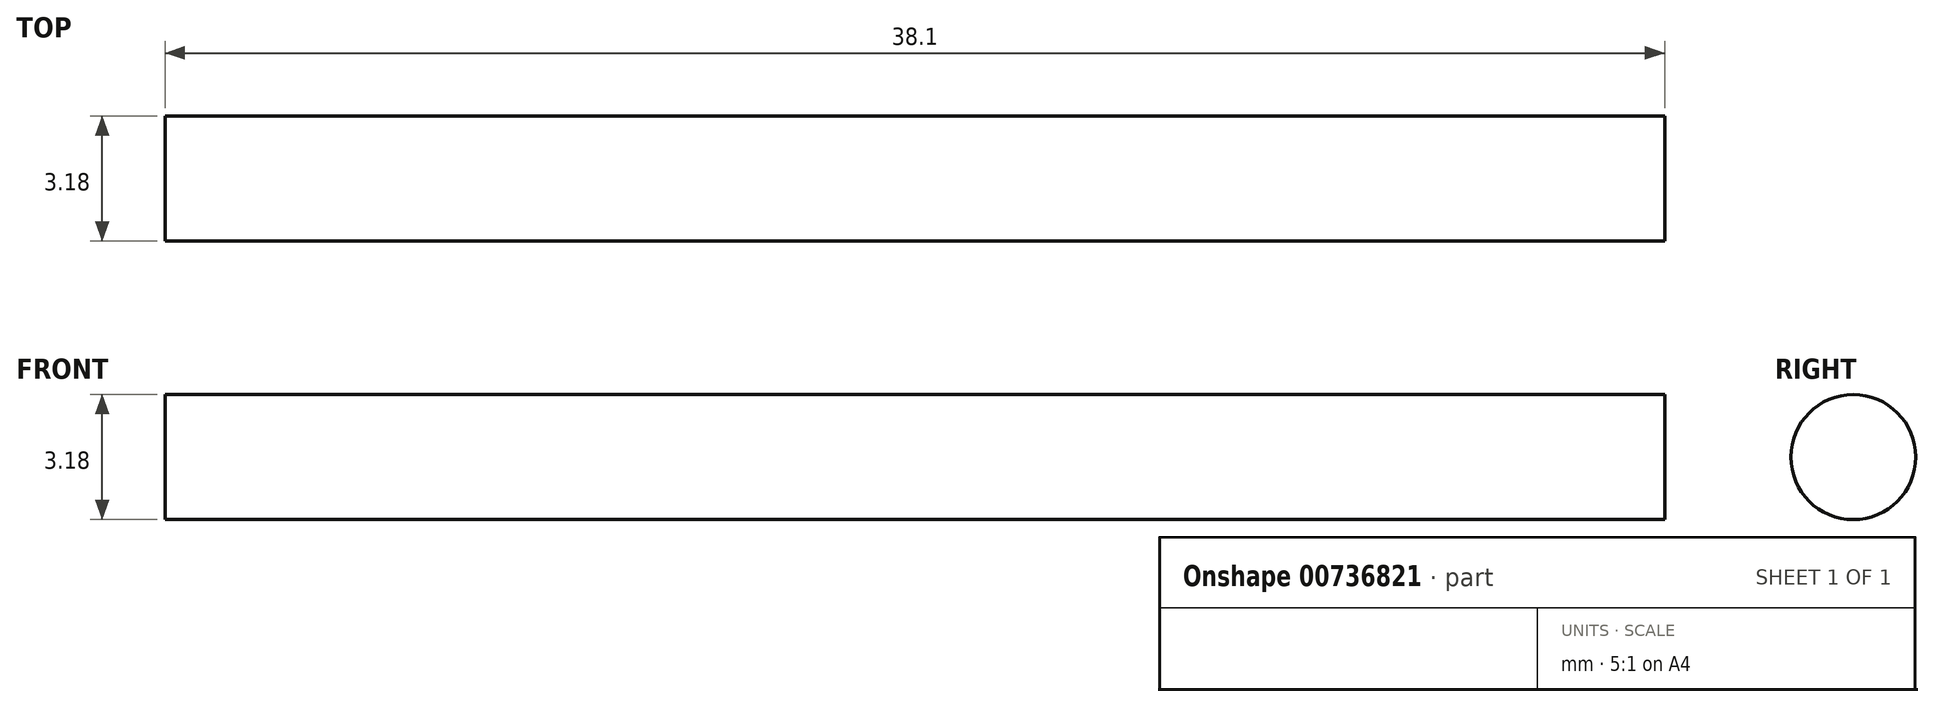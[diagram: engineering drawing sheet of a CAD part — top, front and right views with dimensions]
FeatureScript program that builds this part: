
annotation { "Feature Type Name" : "Feature", "Feature Type Description" : "" }
export const myFeature = defineFeature(function(context is Context, id is Id, definition is map)
    precondition{}
    {
        {
            var Q0;
            Q0=qCreatedBy(makeId("Right.planeOp"),FACE);
            var sketch = newSketch(context, id + "F0", { "sketchPlane" : qUnion([Q0])});
            skCircle(sketch, "E0", {"center": v(0, 0) * mm, "radius": 1.59 * mm});
            skSolve(sketch);
        }
        {
            var Q0;
            Q0=makeQuery(id+"F0.imprint","IMPRINT",FACE,{"disambiguationData":[TD([[makeQuery(id+"F0.imprint","IMPRINT",EDGE,{"derivedFrom":sQuery(id+"F0.wireOp",EDGE,"E0")}),1.0]])]});
            extrude(context, id + "F1", {"entities" : qUnion([Q0]), "depth" : 38.1 * mm, "offsetDistance" : 25.4 * mm});
        }
    });
